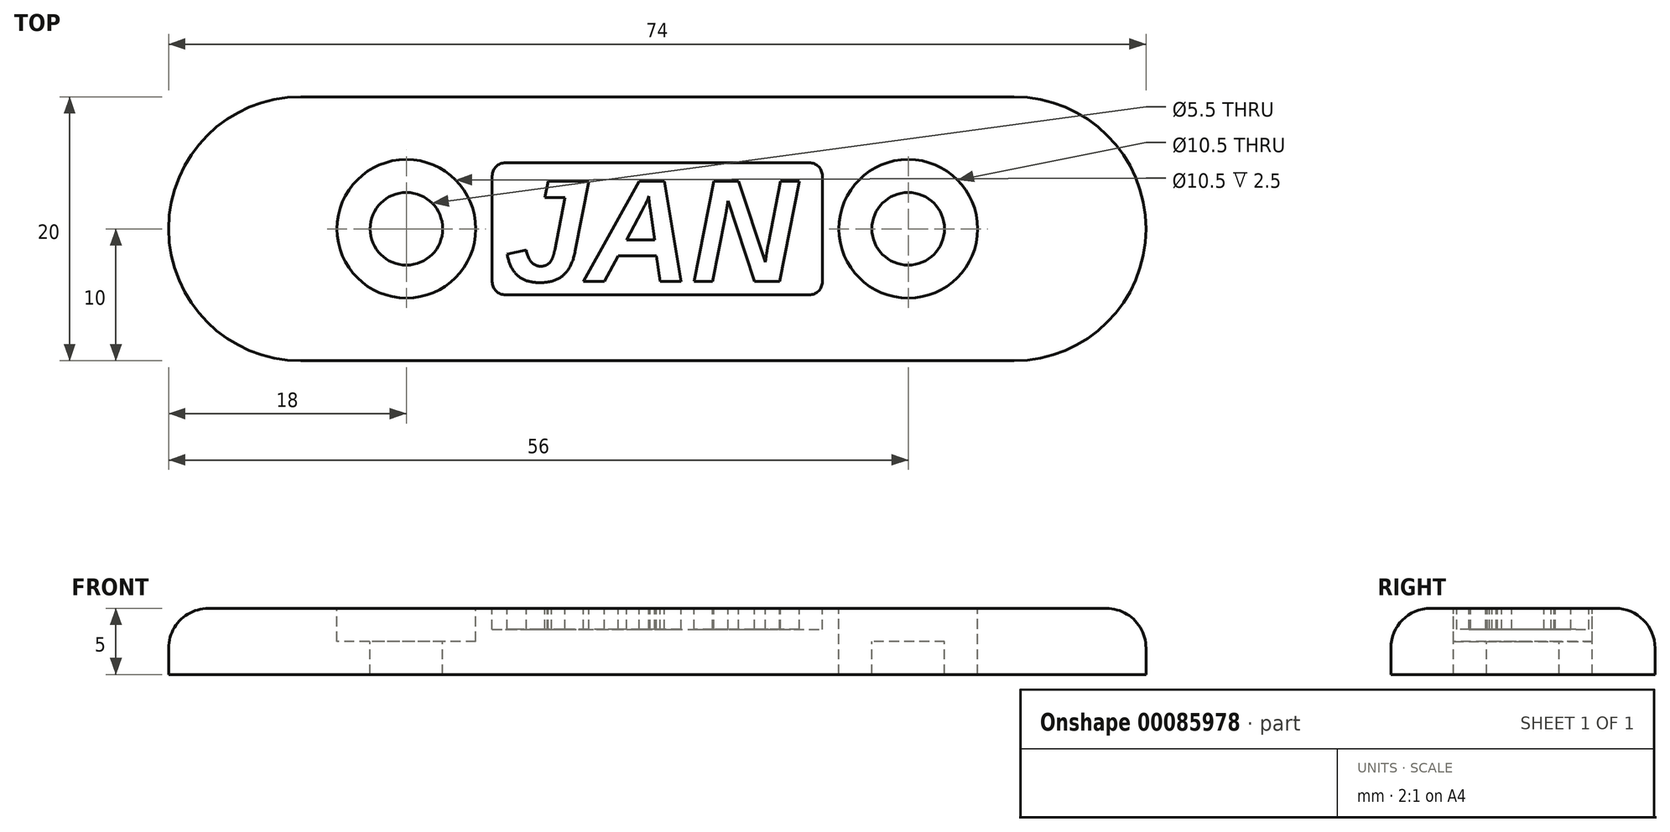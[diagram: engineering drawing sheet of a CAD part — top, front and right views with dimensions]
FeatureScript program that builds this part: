
annotation { "Feature Type Name" : "Feature", "Feature Type Description" : "" }
export const myFeature = defineFeature(function(context is Context, id is Id, definition is map)
    precondition{}
    {
        {
            var Q0;
            Q0=qCreatedBy(makeId("Top.planeOp"),FACE);
            var sketch = newSketch(context, id + "F0", { "sketchPlane" : qUnion([Q0])});
            skArc(sketch, "E0", {"start": v(-27, 10) * mm, "mid": v(-37, 0) * mm, "end": v(-27, -10) * mm});
            skLineSegment(sketch, "E1", {"start": v(0, 21.22) * mm, "end": v(0, -21.27) * mm, "construction": true});
            skArc(sketch, "E2.MirrorC", {"start": v(27, 10) * mm, "mid": v(37, 0) * mm, "end": v(27, -10) * mm});
            skLineSegment(sketch, "E3.bottom", {"start": v(-27, 10) * mm, "end": v(27, 10) * mm});
            skLineSegment(sketch, "E3.top", {"start": v(-27, -10) * mm, "end": v(27, -10) * mm});
            skCircle(sketch, "E4", {"center": v(-19, 0) * mm, "radius": 2.75 * mm});
            skCircle(sketch, "E5.MirrorC", {"center": v(19, 0) * mm, "radius": 2.75 * mm});
            skCircle(sketch, "E6", {"center": v(-19, 0) * mm, "radius": 5.25 * mm});
            skCircle(sketch, "E7.MirrorC", {"center": v(19, 0) * mm, "radius": 5.25 * mm});
            skSolve(sketch);
        }
        {
            var Q0;
            Q0=makeQuery(id+"F0.imprint","IMPRINT",FACE,{"disambiguationData":[TD([[makeQuery(id+"F0.imprint","IMPRINT",EDGE,{"derivedFrom":sQuery(id+"F0.wireOp",EDGE,"E4")}),-1.0]])]});
            var Q1;
            Q1=makeQuery(id+"F0.imprint","IMPRINT",FACE,{"disambiguationData":[TD([[makeQuery(id+"F0.imprint","IMPRINT",EDGE,{"derivedFrom":sQuery(id+"F0.wireOp",EDGE,"E5.MirrorC")}),1.0]])]});
            var Q2;
            Q2=makeQuery(id+"F0.imprint","IMPRINT",FACE,{"disambiguationData":[TD([[makeQuery(id+"F0.imprint","IMPRINT",EDGE,{"derivedFrom":sQuery(id+"F0.wireOp",EDGE,"E0")}),1.0]])]});
            extrude(context, id + "F1", {"entities" : qUnion([Q0, Q1, Q2]), "oppositeDirection" : true, "depth" : 5 * mm});
        }
        {
            var Q0;
            Q0=makeQuery(id+"F0.imprint","IMPRINT",FACE,{"disambiguationData":[TD([[makeQuery(id+"F0.imprint","IMPRINT",EDGE,{"derivedFrom":sQuery(id+"F0.wireOp",EDGE,"E4")}),-1.0]])]});
            var Q1;
            Q1=makeQuery(id+"F0.imprint","IMPRINT",FACE,{"disambiguationData":[TD([[makeQuery(id+"F0.imprint","IMPRINT",EDGE,{"derivedFrom":sQuery(id+"F0.wireOp",EDGE,"E5.MirrorC")}),1.0]])]});
            extrude(context, id + "F2", {"entities" : qUnion([Q0, Q1]), "operationType" : NewBodyOperationType.REMOVE, "oppositeDirection" : true, "depth" : 2.5 * mm});
        }
        {
            var Q0;
            Q0=qCreatedBy(makeId("Front.planeOp"),FACE);
            var sketch = newSketch(context, id + "F3", { "sketchPlane" : qUnion([Q0])});
            skLineSegment(sketch, "E8", {"start": v(-37, -4.78) * mm, "end": v(-37, 0) * mm});
            skLineSegment(sketch, "E9.0.0", {"start": v(27, 0) * mm, "end": v(-27, 0) * mm});
            skLineSegment(sketch, "E9.0.1", {"start": v(-27, 0) * mm, "end": v(-37, 0) * mm});
            skLineSegment(sketch, "E9.0.2", {"start": v(-27, 0) * mm, "end": v(-25, 0) * mm});
            skLineSegment(sketch, "E9.0.3", {"start": v(27, 0) * mm, "end": v(37, 0) * mm});
            skLineSegment(sketch, "E10", {"start": v(37, 0) * mm, "end": v(37, -5) * mm});
            skLineSegment(sketch, "E11", {"start": v(-37, -3.78) * mm, "end": v(-25, 0) * mm});
            skLineSegment(sketch, "E12.MirrorCS", {"start": v(37, -3.78) * mm, "end": v(25, 0) * mm});
            skLineSegment(sketch, "E13.trimOffspring", {"start": v(25, 0) * mm, "end": v(27, 0) * mm});
            skSolve(sketch);
        }
        {
            var Q0;
            Q0=makeQuery(id+"F1.opExtrude","CAP_EDGE",EDGE,{"disambiguationData":[OSD([sQuery(id+"F0.wireOp",EDGE,"E3.top")])],"isStart":true});
            var Q1;
            Q1=makeQuery(id+"F1.opExtrude","CAP_EDGE",EDGE,{"disambiguationData":[OSD([sQuery(id+"F0.wireOp",EDGE,"E3.bottom")])],"isStart":true});
            fillet(context, id + "F4", {"entities" : qUnion([Q0, Q1]), "radius" : 3 * mm, "tangentPropagation" : true, "allowEdgeOverflow" : false});
        }
        {
            var Q0;
            Q0=makeQuery(id+"F1.opExtrude","CAP_FACE",FACE,{"disambiguationData":[OSD([sQuery(id+"F0.wireOp",EDGE,"E0"),sQuery(id+"F0.wireOp",EDGE,"E2.MirrorC"),sQuery(id+"F0.wireOp",EDGE,"E3.bottom"),sQuery(id+"F0.wireOp",EDGE,"E3.top"),sQuery(id+"F0.wireOp",EDGE,"E4"),sQuery(id+"F0.wireOp",EDGE,"E5.MirrorC")])],"isStart":true});
            var sketch = newSketch(context, id + "F5", { "sketchPlane" : qUnion([Q0])});
            skText(sketch, "E14", { "text": "JAN", "fontName": "Arimo-BoldItalic.ttf"});
            skLineSegment(sketch, "E15.bottom", {"start": v(-11.5, 5) * mm, "end": v(11.5, 5) * mm});
            skLineSegment(sketch, "E15.top", {"start": v(-11.5, -5) * mm, "end": v(11.5, -5) * mm});
            skLineSegment(sketch, "E15.left", {"start": v(-12.5, 4) * mm, "end": v(-12.5, -4) * mm});
            skLineSegment(sketch, "E15.right", {"start": v(12.5, 4) * mm, "end": v(12.5, -4) * mm});
            skPoint(sketch, "E16.visualSharp", {"position": v(-12.5, 5) * mm});
            skArc(sketch, "E16.filletArc", {"start": v(-11.5, 5) * mm, "mid": v(-12.2, 4.7) * mm, "end": v(-12.5, 4) * mm});
            skPoint(sketch, "E17.visualSharp", {"position": v(-12.5, -5) * mm});
            skArc(sketch, "E17.filletArc", {"start": v(-12.5, -4) * mm, "mid": v(-12.2, -4.7) * mm, "end": v(-11.5, -5) * mm});
            skPoint(sketch, "E18.visualSharp", {"position": v(12.5, -5) * mm});
            skArc(sketch, "E18.filletArc", {"start": v(11.5, -5) * mm, "mid": v(12.2, -4.7) * mm, "end": v(12.5, -4) * mm});
            skPoint(sketch, "E19.visualSharp", {"position": v(12.5, 5) * mm});
            skArc(sketch, "E19.filletArc", {"start": v(12.5, 4) * mm, "mid": v(12.2, 4.7) * mm, "end": v(11.5, 5) * mm});
            const initialGuessF5  = {"E14": [-0.0115, -0.00397, 1, 0, 0.00794]};
            skSetInitialGuess(sketch, initialGuessF5);
            skSolve(sketch);
        }
        {
            var Q0;
            Q0 = qSketchRegion(id + "F5", true);
            var Q1;
            Q1=makeQuery(id+"F5.imprint","IMPRINT",FACE,{"disambiguationData":[TD([[makeQuery(id+"F5.imprint","IMPRINT",EDGE,{"derivedFrom":sQuery(id+"F5.wireOp",EDGE,"E14.sketch_text.stroke-22")}),1.0]])]});
            extrude(context, id + "F6", {"entities" : qUnion([Q0, Q1]), "operationType" : NewBodyOperationType.REMOVE, "oppositeDirection" : true, "depth" : 1.6 * mm});
        }
    });
